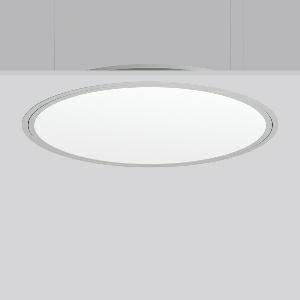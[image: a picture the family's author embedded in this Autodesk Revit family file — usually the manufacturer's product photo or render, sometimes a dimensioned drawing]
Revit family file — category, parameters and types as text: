
# Revit family: triona_round_e_312387_004_1_12_2095
name_source: partatom
category: Lighting Fixtures
units: mm (PartAtom-declared; Revit-internal decimal feet)

## family parameters
Cut with Voids When Loaded = No
Host = Face
Light Source = No
Part Type = Normal
Room Calculation Point = No
Round Connector Dimension = Use Diameter
Shared = No

## types (1)
- TRIONA round E (1 x LED Modul 840, 8300 lm, 4000)
    Apparent Load = 80 VA
    CIE Flux Codes = 49 80 96 100 100
    Color Rendering = 80
    Color Temperature = 4000
    Default Elevation = 1800 mm
    Description = Series: TRIONA round
Decorative round LED recessed surface luminaire. Cover made of sheet steel, powder-coated. Frame made of aluminium, powder-coated. Recessed ring: aluminium extrusion profile, powder coated. Light emission through a diffuser: plastic, opal. Lightguide and diffuser made of non-yellowing plastic (PMMA). Lateral light emission (RZB SIDELITE technology) for above-average homogeneous light distribution. Suitable for installation in cavity ceilings. Tool-free mounting system thanks to the rocker arm mechanism (patent pending). Electronic ballast included. Very easy installation thanks to Plug+Play connection. 
Colour: silver, matt (approx. RAL 9006)
Diameter: 889 mm
Height: 2 mm
Cut-out diameter: 866 mm
Recess height: 100 mm
Luminaire: recess height: 89 mm
Lamp: LED
Socket: without socket
Colour temperature: 4000K
Colour rendering index (CRI): 80
System power: 80 W
Rated luminous flux: 8300 lm
Luminous efficiency: 104 lm/W
Control gear: Converter, dimmable, DALI
Protection class: I
Type of protection: IP 40
    Height = 0 mm  [stored 0 ft]
    Lamp = 1 x LED Modul 840
    Lamp Light Flux = 8300 lm
    Lamp count = 1
    Length = 889 mm
    Lifetime = 50000 h
    Luminous efficacy = 104 lm/W
    Manufacturer = RZB
    ModVariant = No
    Model = 312387.004.1.12
    Mounting Place = Ceiling
    Mounting Type = Recessed
    Number of Poles = 1
    OnlyDefault = Yes
    Power Factor = 1
    Product Name = TRIONA round E
    Product group = Recessed modular luminaires
    ProductGroupID = 406
    Protection Class = Protection class I
    Protection Degree = IP 20
    RLX_Detail_Level = 1
    RLX_Emergency_Light_Flux = 0 lm
    RLX_Emergency_Type = 0
    RLX_Emergency_Type_DB = No
    RlxData = <blob elided: 38817 chars, md5=428d2f74>
    Socket = socket
    Standby Power = 0 W
    System Light Flux = 8300 lm
    System Power = 80 W
    Type Comments = Product without accessories
    Type Image = 312387.004.12.jpg
    URL = http://relux.com
    VarID = ---
    Voltage = 230 V
    Voltage Range = 220-240 V
    Weight = 0.00 kg
    Width = 0 mm  [stored 0 ft]

note: [stored X ft] marks values corroborated as IEEE doubles in the binary element streams (Revit-internal decimal feet)

## geometry (parser evidence)
native form markers: Blend x4, Sweep x11
no freeform markers — native parametric forms only
